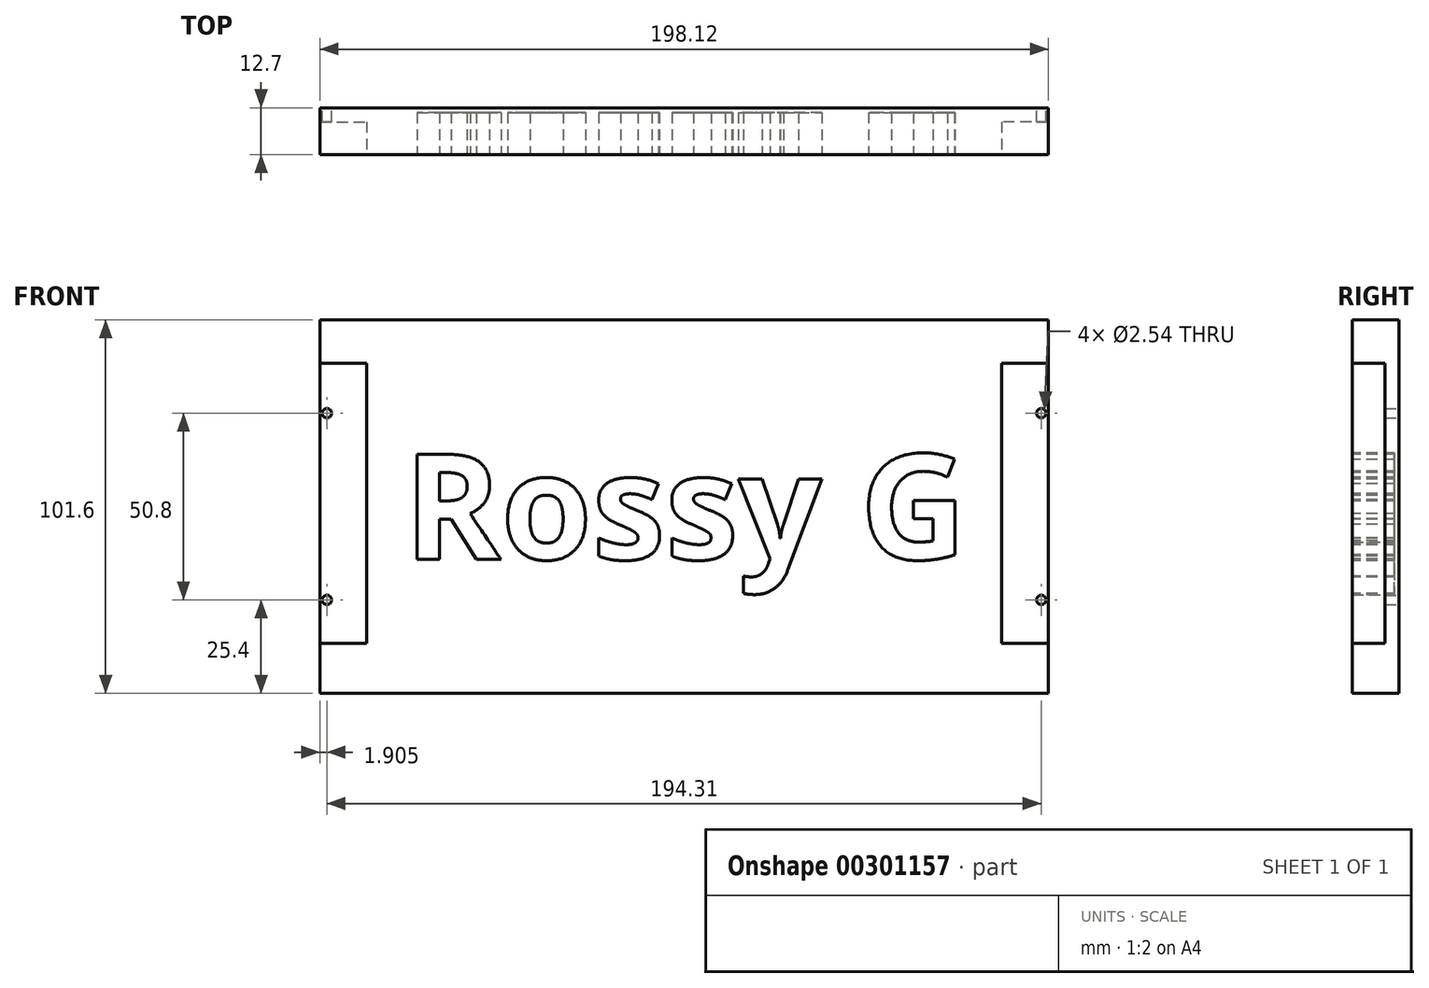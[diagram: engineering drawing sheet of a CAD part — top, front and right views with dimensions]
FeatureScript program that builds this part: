
annotation { "Feature Type Name" : "Feature", "Feature Type Description" : "" }
export const myFeature = defineFeature(function(context is Context, id is Id, definition is map)
    precondition{}
    {
        {
            var Q0;
            Q0=qCreatedBy(makeId("Front.planeOp"),FACE);
            var sketch = newSketch(context, id + "F0", { "sketchPlane" : qUnion([Q0])});
            skLineSegment(sketch, "E0.bottom", {"start": v(99.06, 50.8) * mm, "end": v(-99.06, 50.8) * mm});
            skLineSegment(sketch, "E0.top", {"start": v(99.06, -50.8) * mm, "end": v(-99.06, -50.8) * mm});
            skLineSegment(sketch, "E0.left", {"start": v(99.06, 50.8) * mm, "end": v(99.06, -50.8) * mm});
            skLineSegment(sketch, "E0.right", {"start": v(-99.06, 50.8) * mm, "end": v(-99.06, -50.8) * mm});
            skPoint(sketch, "E0.middle", {"position": v(0, 0) * mm});
            skSolve(sketch);
        }
        {
            var Q0;
            Q0 = qSketchRegion(id + "F0", true);
            extrude(context, id + "F1", {"entities" : qUnion([Q0]), "depth" : 12.7 * mm});
        }
        {
            var Q0;
            Q0=qCreatedBy(makeId("Front.planeOp"),FACE);
            var sketch = newSketch(context, id + "F2", { "sketchPlane" : qUnion([Q0])});
            skCircle(sketch, "E1", {"center": v(-97.16, 25.4) * mm, "radius": 1.27 * mm});
            skCircle(sketch, "E2", {"center": v(-97.16, -25.4) * mm, "radius": 1.27 * mm});
            skCircle(sketch, "E3", {"center": v(97.16, 25.4) * mm, "radius": 1.27 * mm});
            skCircle(sketch, "E4", {"center": v(97.15, -25.4) * mm, "radius": 1.27 * mm});
            skSolve(sketch);
        }
        {
            var Q0;
            Q0 = qSketchRegion(id + "F2", true);
            extrude(context, id + "F3", {"entities" : qUnion([Q0]), "operationType" : NewBodyOperationType.REMOVE, "depth" : 3.8 * mm});
        }
        {
            var Q0;
            Q0=makeQuery(id+"F1.opExtrude","CAP_FACE",FACE,{"disambiguationData":[OSD([sQuery(id+"F0.wireOp",EDGE,"E0.bottom"),sQuery(id+"F0.wireOp",EDGE,"E0.top"),sQuery(id+"F0.wireOp",EDGE,"E0.left"),sQuery(id+"F0.wireOp",EDGE,"E0.right")])],"isStart":false});
            var sketch = newSketch(context, id + "F4", { "sketchPlane" : qUnion([Q0])});
            skText(sketch, "E5", { "text": "Rossy G", "fontName": "OpenSans-Bold.ttf"});
            const initialGuessF4  = {"E5": [-0.0762, -0.01434, 1, 0, 0.0288]};
            skSetInitialGuess(sketch, initialGuessF4);
            skSolve(sketch);
        }
        {
            var Q0;
            Q0 = qSketchRegion(id + "F4", true);
            extrude(context, id + "F5", {"entities" : qUnion([Q0]), "operationType" : NewBodyOperationType.REMOVE, "oppositeDirection" : true, "depth" : 11.43 * mm});
        }
        {
            var Q0;
            {var subQ0=sQuery(id+"F0.wireOp",EDGE,"E0.right");var subQ1=sQuery(id+"F0.wireOp",EDGE,"E0.top");var subQ2=sQuery(id+"F0.wireOp",EDGE,"E0.left");var subQ3=sQuery(id+"F0.wireOp",EDGE,"E0.bottom");Q0=makeQuery(id+"F5.boolean.opBoolean","SPLIT",FACE,{"disambiguationData":[TD([makeQuery(id+"F1.opExtrude","SWEPT_FACE",FACE,{"disambiguationData":[OSD([subQ3])]})])],"derivedFrom":makeQuery(id+"F1.opExtrude","CAP_FACE",FACE,{"disambiguationData":[OSD([subQ3,subQ1,subQ2,subQ0])],"isStart":false})});}
            var sketch = newSketch(context, id + "F6", { "sketchPlane" : qUnion([Q0])});
            skLineSegment(sketch, "E6.bottom", {"start": v(-99.06, 39.01) * mm, "end": v(-86.36, 39.01) * mm});
            skLineSegment(sketch, "E6.top", {"start": v(-99.06, -37.19) * mm, "end": v(-86.36, -37.19) * mm});
            skLineSegment(sketch, "E6.left", {"start": v(-99.06, 39.01) * mm, "end": v(-99.06, -37.19) * mm});
            skLineSegment(sketch, "E6.right", {"start": v(-86.36, 39.01) * mm, "end": v(-86.36, -37.19) * mm});
            skLineSegment(sketch, "E7.bottom", {"start": v(99.06, 39.01) * mm, "end": v(86.36, 39.01) * mm});
            skLineSegment(sketch, "E7.top", {"start": v(99.06, -37.19) * mm, "end": v(86.36, -37.19) * mm});
            skLineSegment(sketch, "E7.left", {"start": v(99.06, 39.01) * mm, "end": v(99.06, -37.19) * mm});
            skLineSegment(sketch, "E7.right", {"start": v(86.36, 39.01) * mm, "end": v(86.36, -37.19) * mm});
            skSolve(sketch);
        }
        {
            var Q0;
            Q0 = qSketchRegion(id + "F6", true);
            extrude(context, id + "F7", {"entities" : qUnion([Q0]), "operationType" : NewBodyOperationType.REMOVE, "oppositeDirection" : true, "depth" : 8.9 * mm});
        }
    });
